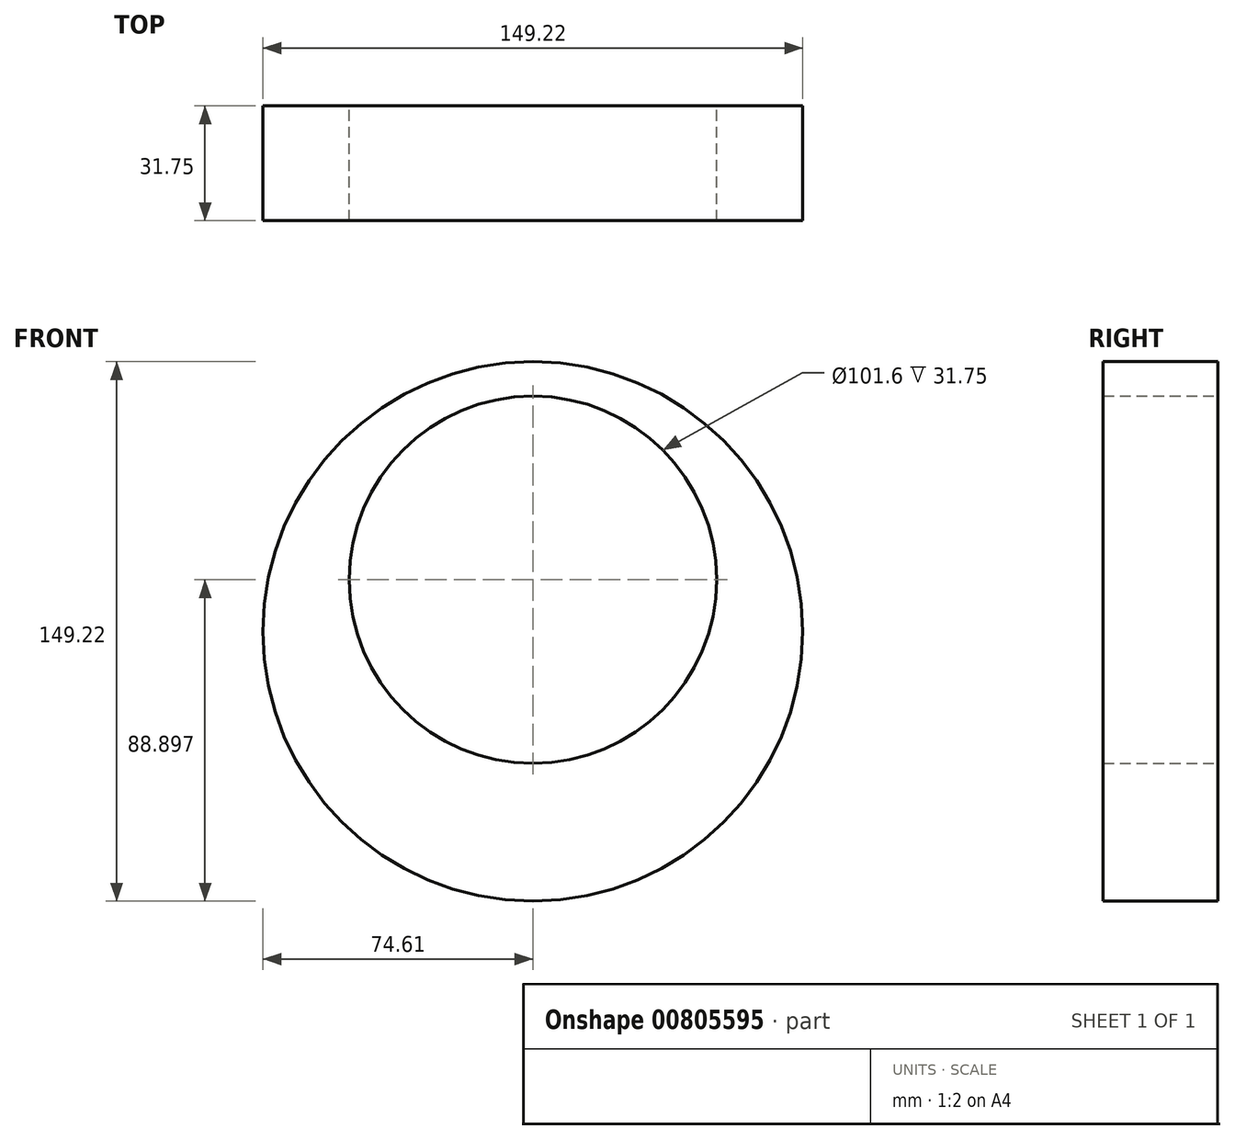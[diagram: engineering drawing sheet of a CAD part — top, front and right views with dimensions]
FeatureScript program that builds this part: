
annotation { "Feature Type Name" : "Feature", "Feature Type Description" : "" }
export const myFeature = defineFeature(function(context is Context, id is Id, definition is map)
    precondition{}
    {
        {
            var Q0;
            Q0=qCreatedBy(makeId("Front.planeOp"),FACE);
            var sketch = newSketch(context, id + "F0", { "sketchPlane" : qUnion([Q0])});
            skCircle(sketch, "E0", {"center": v(0, 0) * mm, "radius": 74.61 * mm});
            skCircle(sketch, "E1", {"center": v(0, 14.29) * mm, "radius": 50.8 * mm});
            skSolve(sketch);
        }
        {
            var Q0;
            Q0=makeQuery(id+"F0.imprint","IMPRINT",FACE,{"disambiguationData":[TD([[makeQuery(id+"F0.imprint","IMPRINT",EDGE,{"derivedFrom":sQuery(id+"F0.wireOp",EDGE,"E0")}),1.0]])]});
            extrude(context, id + "F1", {"entities" : qUnion([Q0]), "depth" : 31.75 * mm, "offsetDistance" : 25.4 * mm});
        }
    });
